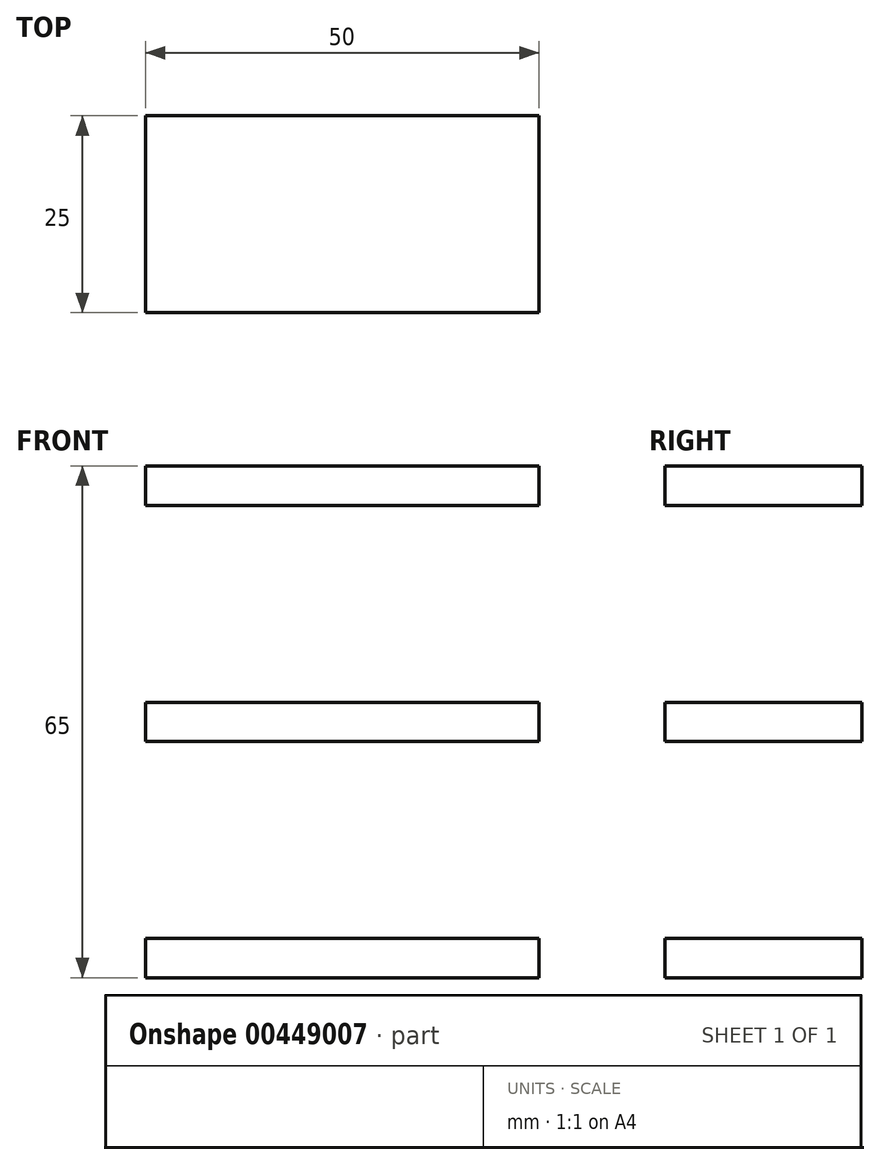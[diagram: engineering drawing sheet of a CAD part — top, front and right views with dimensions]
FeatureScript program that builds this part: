
annotation { "Feature Type Name" : "Feature", "Feature Type Description" : "" }
export const myFeature = defineFeature(function(context is Context, id is Id, definition is map)
    precondition{}
    {
        {
            var Q0;
            Q0=qCreatedBy(makeId("Front.planeOp"),FACE);
            var sketch = newSketch(context, id + "F0", { "sketchPlane" : qUnion([Q0])});
            skLineSegment(sketch, "E0.bottom", {"start": v(0, -32.5) * mm, "end": v(50, -32.5) * mm});
            skLineSegment(sketch, "E0.top", {"start": v(0, -27.5) * mm, "end": v(50, -27.5) * mm});
            skLineSegment(sketch, "E0.left", {"start": v(0, -32.5) * mm, "end": v(0, -27.5) * mm});
            skLineSegment(sketch, "E0.right", {"start": v(50, -32.5) * mm, "end": v(50, -27.5) * mm});
            skLineSegment(sketch, "E1.bottom", {"start": v(0, -27.5) * mm, "end": v(5, -27.5) * mm});
            skLineSegment(sketch, "E1.top", {"start": v(0, -2.5) * mm, "end": v(5, -2.5) * mm});
            skLineSegment(sketch, "E1.left", {"start": v(0, -27.5) * mm, "end": v(0, -2.5) * mm});
            skLineSegment(sketch, "E1.right", {"start": v(5, -27.5) * mm, "end": v(5, -2.5) * mm});
            skLineSegment(sketch, "E2.bottom", {"start": v(0, -2.5) * mm, "end": v(50, -2.5) * mm});
            skLineSegment(sketch, "E2.top", {"start": v(0, 2.5) * mm, "end": v(50, 2.5) * mm});
            skLineSegment(sketch, "E2.left", {"start": v(0, -2.5) * mm, "end": v(0, 2.5) * mm});
            skLineSegment(sketch, "E2.right", {"start": v(50, -2.5) * mm, "end": v(50, 2.5) * mm});
            skLineSegment(sketch, "E3.bottom", {"start": v(0, 2.5) * mm, "end": v(5, 2.5) * mm});
            skLineSegment(sketch, "E3.top", {"start": v(0, 27.5) * mm, "end": v(5, 27.5) * mm});
            skLineSegment(sketch, "E3.left", {"start": v(0, 2.5) * mm, "end": v(0, 27.5) * mm});
            skLineSegment(sketch, "E3.right", {"start": v(5, 2.5) * mm, "end": v(5, 27.5) * mm});
            skLineSegment(sketch, "E4.bottom", {"start": v(0, 27.5) * mm, "end": v(50, 27.5) * mm});
            skLineSegment(sketch, "E4.top", {"start": v(0, 32.5) * mm, "end": v(50, 32.5) * mm});
            skLineSegment(sketch, "E4.left", {"start": v(0, 27.5) * mm, "end": v(0, 32.5) * mm});
            skLineSegment(sketch, "E4.right", {"start": v(50, 27.5) * mm, "end": v(50, 32.5) * mm});
            skPoint(sketch, "E5", {"position": v(0, 0) * mm});
            skSolve(sketch);
        }
        {
            var Q0;
            Q0=makeQuery(id+"F0.imprint","IMPRINT",FACE,{"disambiguationData":[TD([[makeQuery(id+"F0.imprint","IMPRINT",EDGE,{"derivedFrom":sQuery(id+"F0.wireOp",EDGE,"E0.bottom")}),1.0]])]});
            extrude(context, id + "F1", {"entities" : qUnion([Q0]), "depth" : 25 * mm});
        }
        {
            var Q0;
            Q0=makeQuery(id+"F0.imprint","IMPRINT",FACE,{"disambiguationData":[TD([[makeQuery(id+"F0.imprint","IMPRINT",EDGE,{"derivedFrom":sQuery(id+"F0.wireOp",EDGE,"E2.top")}),-1.0]])]});
            var Q1;
            Q1=makeQuery(id+"F1.opExtrude","CAP_FACE",FACE,{"disambiguationData":[OSD([sQuery(id+"F0.wireOp",EDGE,"E0.bottom"),sQuery(id+"F0.wireOp",EDGE,"E0.top"),sQuery(id+"F0.wireOp",EDGE,"E0.left"),sQuery(id+"F0.wireOp",EDGE,"E0.right"),sQuery(id+"F0.wireOp",EDGE,"E1.left"),sQuery(id+"F0.wireOp",EDGE,"E1.right"),sQuery(id+"F0.wireOp",EDGE,"E2.bottom")])],"isStart":false});
            extrude(context, id + "F2", {"entities" : qUnion([Q0]), "endBound" : BoundingType.UP_TO_SURFACE, "endBoundEntityFace" : qUnion([Q1]), "depth" : 2 * mm});
        }
        {
            var Q0;
            Q0=makeQuery(id+"F0.imprint","IMPRINT",FACE,{"disambiguationData":[TD([[makeQuery(id+"F0.imprint","IMPRINT",EDGE,{"derivedFrom":sQuery(id+"F0.wireOp",EDGE,"E4.top")}),-1.0]])]});
            var Q1;
            Q1=makeQuery(id+"F1.opExtrude","CAP_FACE",FACE,{"disambiguationData":[OSD([sQuery(id+"F0.wireOp",EDGE,"E0.bottom"),sQuery(id+"F0.wireOp",EDGE,"E0.top"),sQuery(id+"F0.wireOp",EDGE,"E0.left"),sQuery(id+"F0.wireOp",EDGE,"E0.right"),sQuery(id+"F0.wireOp",EDGE,"E1.left"),sQuery(id+"F0.wireOp",EDGE,"E1.right"),sQuery(id+"F0.wireOp",EDGE,"E2.bottom")])],"isStart":false});
            extrude(context, id + "F3", {"entities" : qUnion([Q0]), "endBound" : BoundingType.UP_TO_SURFACE, "endBoundEntityFace" : qUnion([Q1]), "depth" : 25 * mm});
        }
    });
